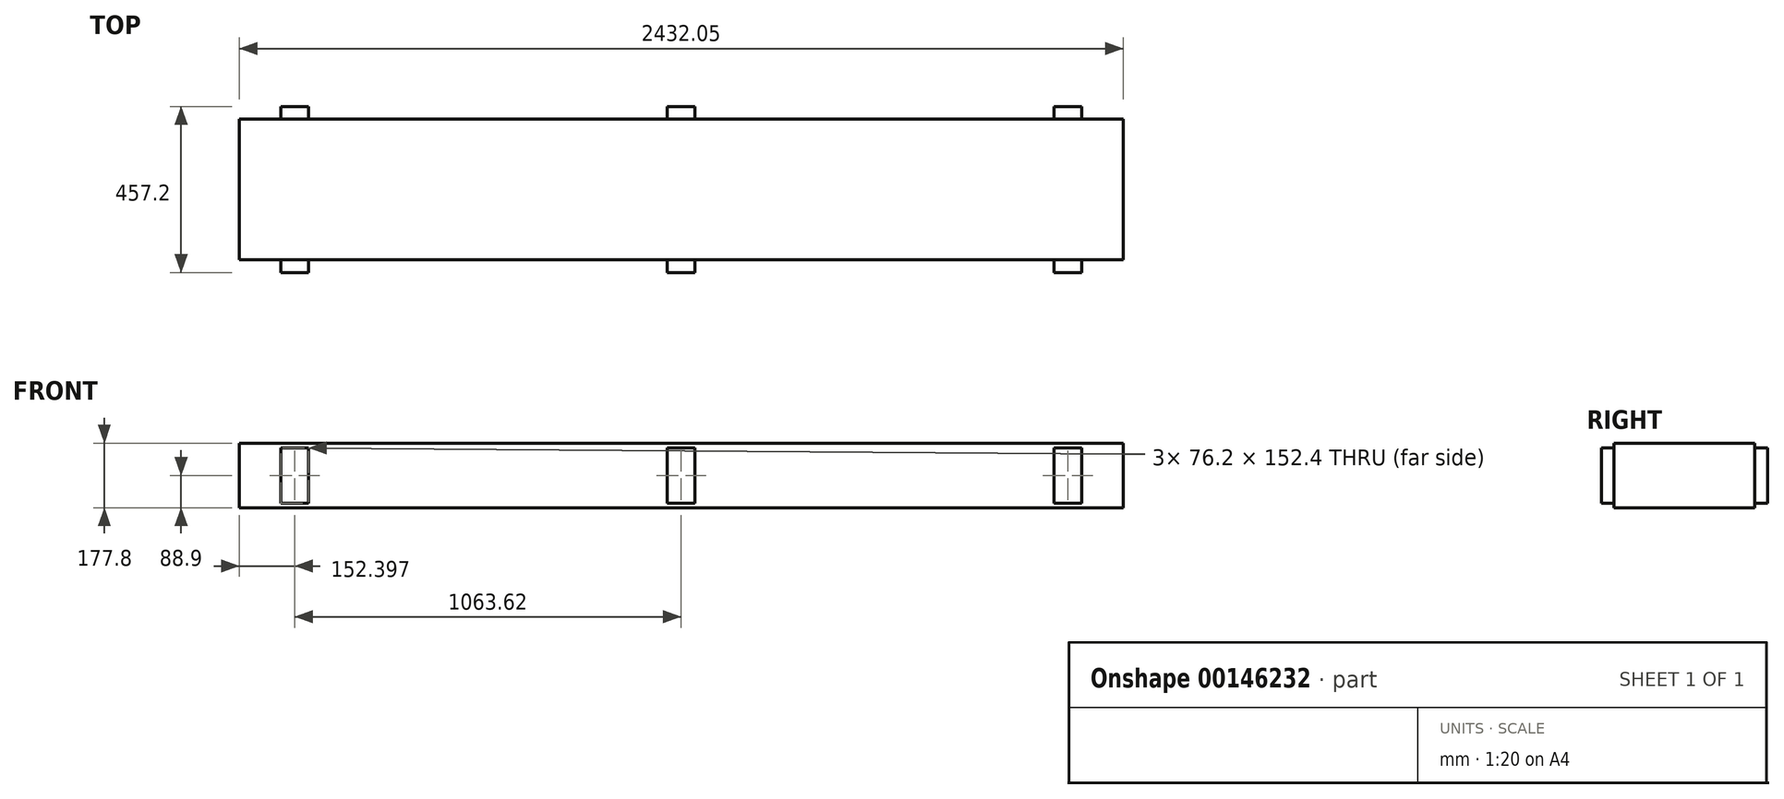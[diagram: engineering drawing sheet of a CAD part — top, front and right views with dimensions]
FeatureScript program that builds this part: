
annotation { "Feature Type Name" : "Feature", "Feature Type Description" : "" }
export const myFeature = defineFeature(function(context is Context, id is Id, definition is map)
    precondition{}
    {
        {
            var Q0;
            Q0=qCreatedBy(makeId("Top.planeOp"),FACE);
            var sketch = newSketch(context, id + "F0", { "sketchPlane" : qUnion([Q0])});
            skLineSegment(sketch, "E0.bottom", {"start": v(-445.27, 192.2) * mm, "end": v(1986.78, 192.2) * mm});
            skLineSegment(sketch, "E0.top", {"start": v(-445.27, -195.14) * mm, "end": v(1986.78, -195.14) * mm});
            skLineSegment(sketch, "E0.left", {"start": v(-445.27, 192.2) * mm, "end": v(-445.27, -195.14) * mm});
            skLineSegment(sketch, "E0.right", {"start": v(1986.78, 192.2) * mm, "end": v(1986.78, -195.14) * mm});
            skSolve(sketch);
        }
        {
            var Q0;
            Q0=makeQuery(id+"F0.imprint","IMPRINT",FACE,{"disambiguationData":[TD([[makeQuery(id+"F0.imprint","IMPRINT",EDGE,{"derivedFrom":sQuery(id+"F0.wireOp",EDGE,"E0.bottom")}),-1.0]])]});
            extrude(context, id + "F1", {"entities" : qUnion([Q0]), "depth" : 177.8 * mm});
        }
        {
            var Q0;
            Q0=makeQuery(id+"F1.opExtrude","SWEPT_FACE",FACE,{"disambiguationData":[OSD([sQuery(id+"F0.wireOp",EDGE,"E0.top")])]});
            var sketch = newSketch(context, id + "F6", { "sketchPlane" : qUnion([Q0])});
            skLineSegment(sketch, "E1.bottom", {"start": v(-330.97, 165.1) * mm, "end": v(-254.77, 165.1) * mm});
            skLineSegment(sketch, "E1.top", {"start": v(-330.97, 12.7) * mm, "end": v(-254.77, 12.7) * mm});
            skLineSegment(sketch, "E1.left", {"start": v(-330.97, 165.1) * mm, "end": v(-330.97, 12.7) * mm});
            skLineSegment(sketch, "E1.right", {"start": v(-254.77, 165.1) * mm, "end": v(-254.77, 12.7) * mm});
            skSolve(sketch);
        }
        {
            var Q0;
            Q0=makeQuery(id+"F6.imprint","IMPRINT",FACE,{"disambiguationData":[TD([[makeQuery(id+"F6.imprint","IMPRINT",EDGE,{"derivedFrom":sQuery(id+"F6.wireOp",EDGE,"E1.bottom")}),-1.0]])]});
            extrude(context, id + "F7", {"entities" : qUnion([Q0]), "operationType" : NewBodyOperationType.ADD, "depth" : 34.92 * mm});
        }
        {
            var Q0;
            Q0=makeQuery(id+"F1.opExtrude","SWEPT_FACE",FACE,{"disambiguationData":[OSD([sQuery(id+"F0.wireOp",EDGE,"E0.top")])]});
            var sketch = newSketch(context, id + "F2", { "sketchPlane" : qUnion([Q0])});
            skLineSegment(sketch, "E2.bottom", {"start": v(1872.48, 165.1) * mm, "end": v(1796.28, 165.1) * mm});
            skLineSegment(sketch, "E2.top", {"start": v(1872.48, 12.7) * mm, "end": v(1796.28, 12.7) * mm});
            skLineSegment(sketch, "E2.left", {"start": v(1872.48, 165.1) * mm, "end": v(1872.48, 12.7) * mm});
            skLineSegment(sketch, "E2.right", {"start": v(1796.28, 165.1) * mm, "end": v(1796.28, 12.7) * mm});
            skSolve(sketch);
        }
        {
            var Q0;
            Q0=makeQuery(id+"F2.imprint","IMPRINT",FACE,{"disambiguationData":[TD([[makeQuery(id+"F2.imprint","IMPRINT",EDGE,{"derivedFrom":sQuery(id+"F2.wireOp",EDGE,"E2.bottom")}),1.0]])]});
            extrude(context, id + "F3", {"entities" : qUnion([Q0]), "operationType" : NewBodyOperationType.ADD, "depth" : 34.92 * mm});
        }
        {
            var Q0;
            Q0=makeQuery(id+"F2.imprint","IMPRINT",FACE,{"disambiguationData":[TD([[makeQuery(id+"F2.imprint","IMPRINT",EDGE,{"derivedFrom":sQuery(id+"F2.wireOp",EDGE,"E2.bottom")}),1.0]])]});
            extrude(context, id + "F8", {"entities" : qUnion([Q0]), "operationType" : NewBodyOperationType.ADD, "oppositeDirection" : true, "depth" : 422.27 * mm});
        }
        {
            var Q0;
            Q0=makeQuery(id+"F6.imprint","IMPRINT",FACE,{"disambiguationData":[TD([[makeQuery(id+"F6.imprint","IMPRINT",EDGE,{"derivedFrom":sQuery(id+"F6.wireOp",EDGE,"E1.bottom")}),-1.0]])]});
            extrude(context, id + "F9", {"entities" : qUnion([Q0]), "operationType" : NewBodyOperationType.ADD, "oppositeDirection" : true, "depth" : 422.27 * mm});
        }
        {
            var Q0;
            Q0=makeQuery(id+"F2.imprint","IMPRINT",FACE,{"disambiguationData":[TD([[makeQuery(id+"F2.imprint","IMPRINT",EDGE,{"derivedFrom":sQuery(id+"F2.wireOp",EDGE,"E2.bottom")}),-1.0]])]});
            var sketch = newSketch(context, id + "F4", { "sketchPlane" : qUnion([Q0])});
            skLineSegment(sketch, "E3.bottom", {"start": v(732.65, 165.1) * mm, "end": v(808.85, 165.1) * mm});
            skLineSegment(sketch, "E3.top", {"start": v(732.65, 12.7) * mm, "end": v(808.85, 12.7) * mm});
            skLineSegment(sketch, "E3.left", {"start": v(732.65, 165.1) * mm, "end": v(732.65, 12.7) * mm});
            skLineSegment(sketch, "E3.right", {"start": v(808.85, 165.1) * mm, "end": v(808.85, 12.7) * mm});
            skSolve(sketch);
        }
        {
            var Q0;
            Q0=makeQuery(id+"F4.imprint","IMPRINT",FACE,{"disambiguationData":[TD([[makeQuery(id+"F4.imprint","IMPRINT",EDGE,{"derivedFrom":sQuery(id+"F4.wireOp",EDGE,"E3.bottom")}),-1.0]])]});
            extrude(context, id + "F10", {"entities" : qUnion([Q0]), "operationType" : NewBodyOperationType.ADD, "depth" : 34.92 * mm});
        }
        {
            var Q0;
            Q0=makeQuery(id+"F4.imprint","IMPRINT",FACE,{"disambiguationData":[TD([[makeQuery(id+"F4.imprint","IMPRINT",EDGE,{"derivedFrom":sQuery(id+"F4.wireOp",EDGE,"E3.bottom")}),-1.0]])]});
            extrude(context, id + "F5", {"entities" : qUnion([Q0]), "operationType" : NewBodyOperationType.ADD, "oppositeDirection" : true, "depth" : 422.27 * mm});
        }
    });
